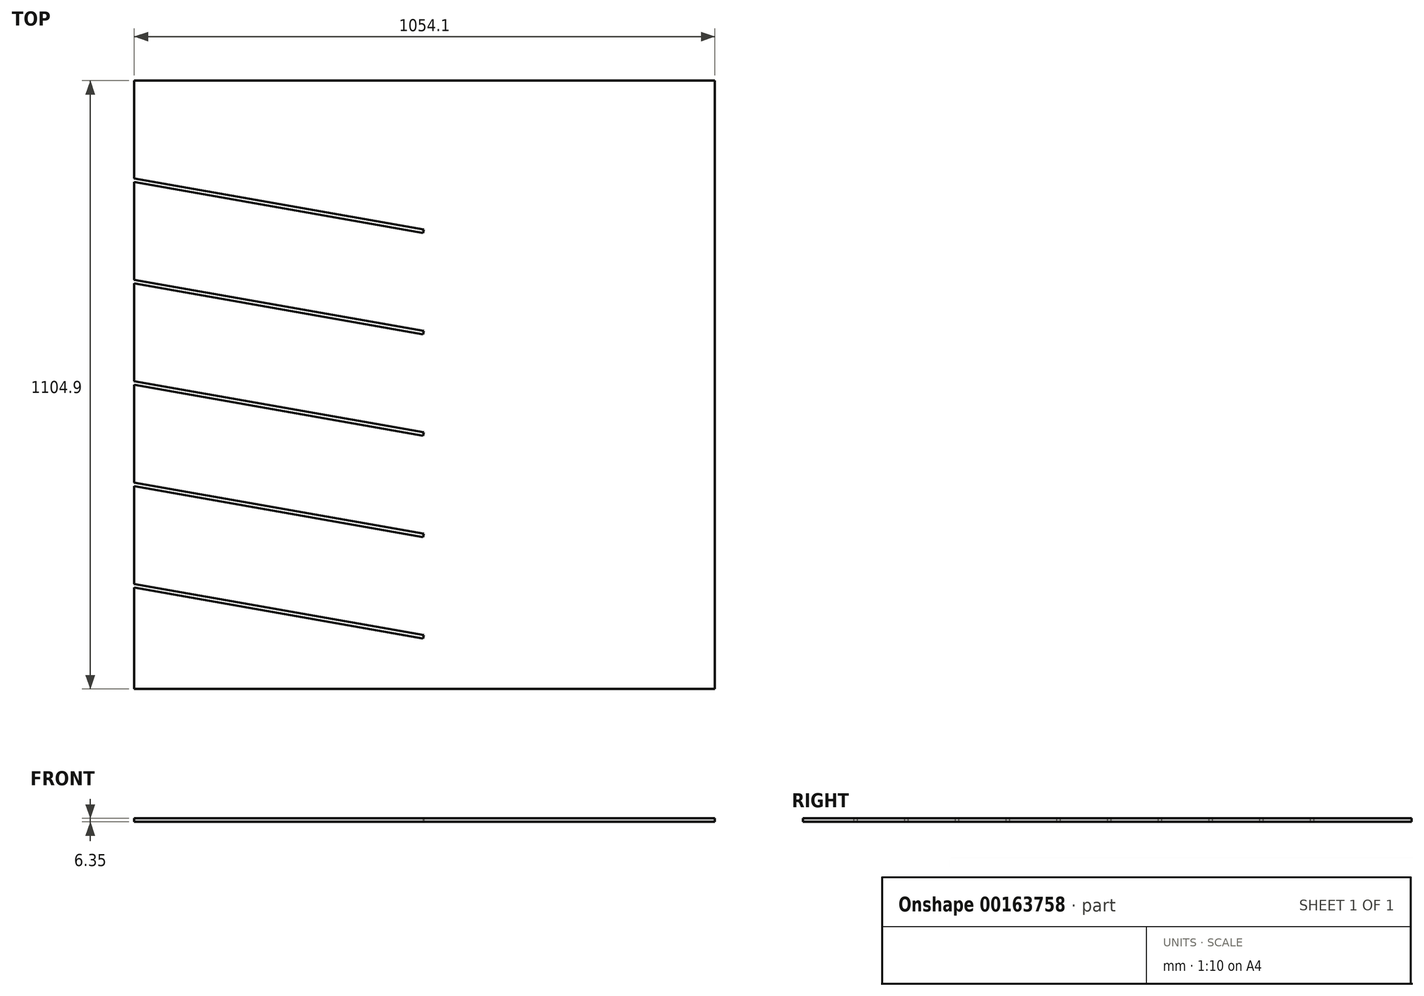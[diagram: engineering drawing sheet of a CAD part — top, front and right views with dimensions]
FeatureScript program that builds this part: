
annotation { "Feature Type Name" : "Feature", "Feature Type Description" : "" }
export const myFeature = defineFeature(function(context is Context, id is Id, definition is map)
    precondition{}
    {
        {
            var Q0;
            Q0=qCreatedBy(makeId("Top.planeOp"),FACE);
            var sketch = newSketch(context, id + "F0", { "sketchPlane" : qUnion([Q0])});
            skLineSegment(sketch, "E0.bottom", {"start": v(-968.94, 1037.94) * mm, "end": v(85.16, 1037.94) * mm});
            skLineSegment(sketch, "E0.top", {"start": v(-968.94, -66.96) * mm, "end": v(85.16, -66.96) * mm});
            skLineSegment(sketch, "E0.left", {"start": v(-968.94, 1037.94) * mm, "end": v(-968.94, 860.14) * mm});
            skLineSegment(sketch, "E0.right", {"start": v(85.16, 1037.94) * mm, "end": v(85.16, -66.96) * mm});
            skLineSegment(sketch, "E1", {"start": v(-968.94, 1031.59) * mm, "end": v(-968.94, 865.47) * mm});
            skLineSegment(sketch, "E2", {"start": v(-968.94, 846.12) * mm, "end": v(-968.94, 681.32) * mm});
            skLineSegment(sketch, "E3", {"start": v(-968.94, 669.64) * mm, "end": v(-968.94, 491.84) * mm});
            skLineSegment(sketch, "E4", {"start": v(-968.94, 485.49) * mm, "end": v(-968.94, 307.69) * mm});
            skLineSegment(sketch, "E5", {"start": v(-968.94, 301.34) * mm, "end": v(-968.94, 123.54) * mm});
            skLineSegment(sketch, "E6", {"start": v(-968.94, 860.14) * mm, "end": v(-443.64, 767.51) * mm});
            skLineSegment(sketch, "E7", {"start": v(-968.94, 675.99) * mm, "end": v(-443.64, 583.36) * mm});
            skLineSegment(sketch, "E8", {"start": v(-968.94, 491.84) * mm, "end": v(-443.64, 399.21) * mm});
            skLineSegment(sketch, "E9", {"start": v(-968.94, 307.69) * mm, "end": v(-443.64, 215.06) * mm});
            skLineSegment(sketch, "E10", {"start": v(-968.94, 123.54) * mm, "end": v(-443.64, 30.91) * mm});
            skLineSegment(sketch, "E11.0", {"start": v(-968.94, 117.09) * mm, "end": v(-444.74, 24.66) * mm});
            skLineSegment(sketch, "E12.0", {"start": v(-968.94, 301.24) * mm, "end": v(-444.74, 208.81) * mm});
            skLineSegment(sketch, "E13.0", {"start": v(-968.94, 485.39) * mm, "end": v(-444.74, 392.96) * mm});
            skLineSegment(sketch, "E14.0", {"start": v(-968.94, 669.54) * mm, "end": v(-444.74, 577.11) * mm});
            skLineSegment(sketch, "E15.0", {"start": v(-968.94, 853.69) * mm, "end": v(-444.74, 761.26) * mm});
            skLineSegment(sketch, "E16.trimOffspring", {"start": v(-968.94, 853.79) * mm, "end": v(-968.94, 675.99) * mm});
            skLineSegment(sketch, "E17.trimOffspring", {"start": v(-968.94, 661.97) * mm, "end": v(-968.94, 497.17) * mm});
            skLineSegment(sketch, "E18.trimOffspring", {"start": v(-968.94, 477.82) * mm, "end": v(-968.94, 313.02) * mm});
            skLineSegment(sketch, "E19.trimOffspring", {"start": v(-968.94, 293.67) * mm, "end": v(-968.94, 123.54) * mm});
            skLineSegment(sketch, "E20.trimOffspring", {"start": v(-968.94, 117.09) * mm, "end": v(-968.94, -66.96) * mm});
            skLineSegment(sketch, "E21", {"start": v(-444.74, 24.66) * mm, "end": v(-443.64, 30.91) * mm});
            skLineSegment(sketch, "E22", {"start": v(-444.74, 208.81) * mm, "end": v(-443.64, 215.06) * mm});
            skLineSegment(sketch, "E23", {"start": v(-444.74, 392.96) * mm, "end": v(-443.64, 399.21) * mm});
            skLineSegment(sketch, "E24", {"start": v(-444.74, 577.11) * mm, "end": v(-443.64, 583.36) * mm});
            skLineSegment(sketch, "E25", {"start": v(-444.74, 761.26) * mm, "end": v(-443.64, 767.51) * mm});
            skPoint(sketch, "E26.visualSharp", {"position": v(-968.94, 860.14) * mm});
            skPoint(sketch, "E27.newPointB", {"position": v(-968.94, 853.79) * mm});
            skPoint(sketch, "E28.visualSharp", {"position": v(-968.94, 675.99) * mm});
            skPoint(sketch, "E29.visualSharp", {"position": v(-968.94, 491.84) * mm});
            skPoint(sketch, "E30.visualSharp", {"position": v(-968.94, 307.69) * mm});
            skPoint(sketch, "E31.visualSharp", {"position": v(-968.94, 123.54) * mm});
            skPoint(sketch, "E32.visualSharp", {"position": v(-968.94, -66.96) * mm});
            skPoint(sketch, "E33.visualSharp", {"position": v(-968.94, 1037.94) * mm});
            skSolve(sketch);
        }
        {
            var Q0;
            Q0 = qSketchRegion(id + "F0", true);
            extrude(context, id + "F1", {"entities" : qUnion([Q0]), "depth" : 6.35 * mm, "offsetDistance" : 25.4 * mm});
        }
    });
